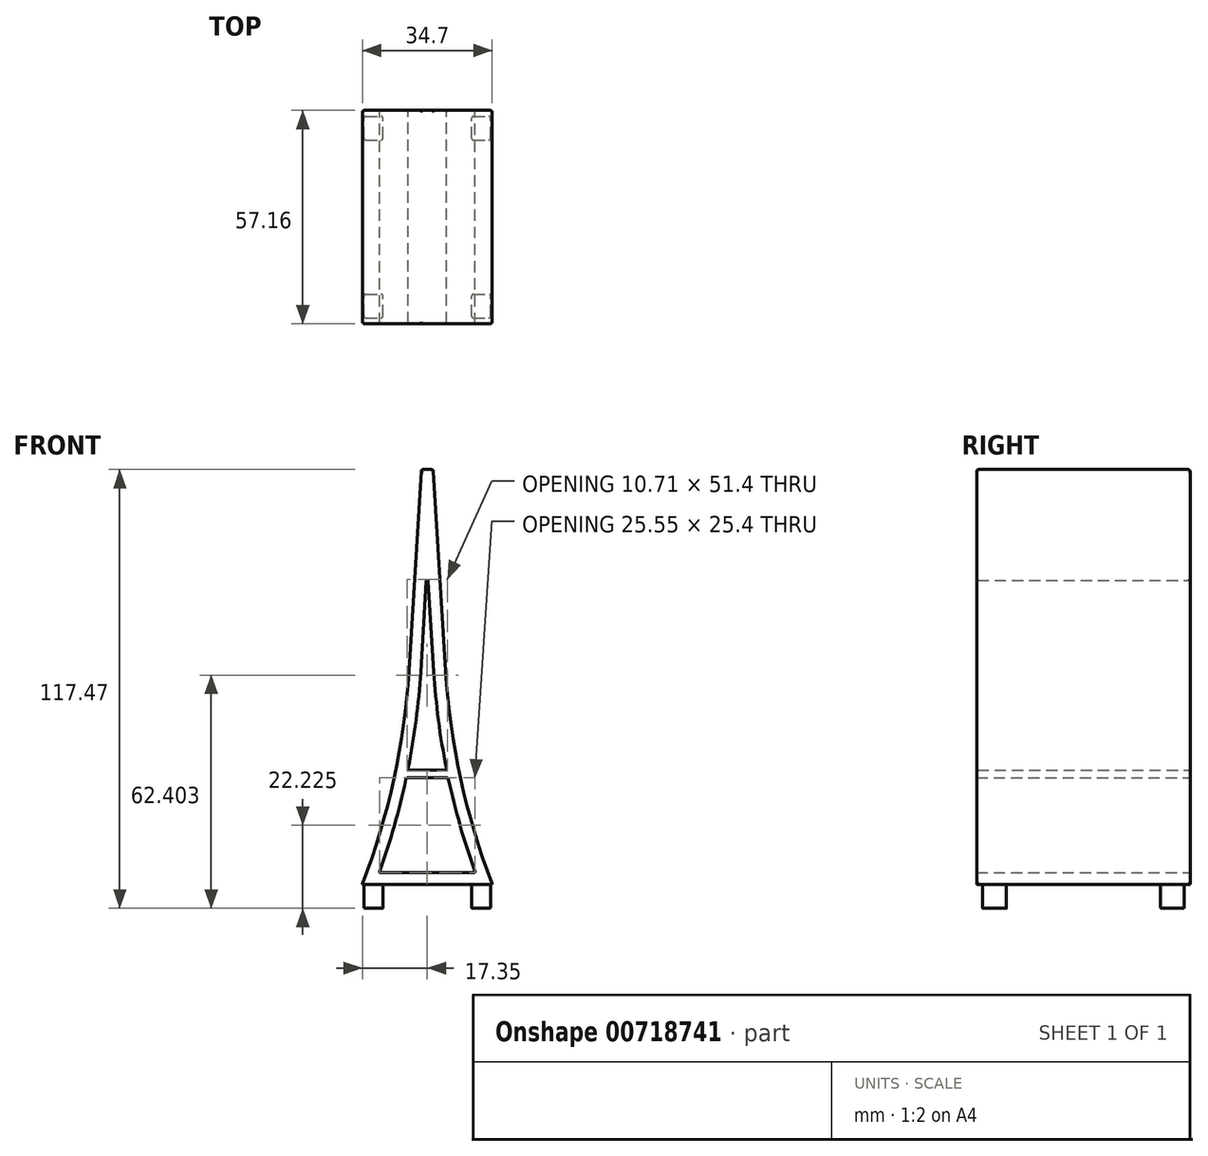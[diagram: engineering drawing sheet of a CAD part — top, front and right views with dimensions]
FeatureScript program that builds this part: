
annotation { "Feature Type Name" : "Feature", "Feature Type Description" : "" }
export const myFeature = defineFeature(function(context is Context, id is Id, definition is map)
    precondition{}
    {
        {
            var Q0;
            Q0=qCreatedBy(makeId("Front.planeOp"),FACE);
            var sketch = newSketch(context, id + "F0", { "sketchPlane" : qUnion([Q0])});
            skLineSegment(sketch, "E0", {"start": v(0, 0) * mm, "end": v(0, 107.5) * mm, "construction": true});
            skLineSegment(sketch, "E1", {"start": v(-17.46, 0) * mm, "end": v(17.46, 0) * mm});
            skLineSegment(sketch, "E2", {"start": v(-1.59, 111.13) * mm, "end": v(1.59, 111.13) * mm});
            skLineSegment(sketch, "E3", {"start": v(-1.59, 111.13) * mm, "end": v(-4.93, 57.15) * mm});
            skArc(sketch, "E4", {"start": v(-4.93, 57.15) * mm, "mid": v(-8.99, 28.1) * mm, "end": v(-17.46, 0) * mm});
            skLineSegment(sketch, "E5.MirrorCS", {"start": v(1.59, 111.13) * mm, "end": v(4.93, 57.15) * mm});
            skArc(sketch, "E6.MirrorCS", {"start": v(4.93, 57.15) * mm, "mid": v(8.99, 28.1) * mm, "end": v(17.46, 0) * mm});
            skLineSegment(sketch, "E7.top", {"start": v(-16.95, -6.35) * mm, "end": v(-11.87, -6.35) * mm});
            skLineSegment(sketch, "E7.left", {"start": v(-16.95, 0) * mm, "end": v(-16.95, -6.35) * mm});
            skLineSegment(sketch, "E7.right", {"start": v(-11.87, 0) * mm, "end": v(-11.87, -6.35) * mm});
            skLineSegment(sketch, "E8.MirrorCS", {"start": v(11.87, 0) * mm, "end": v(11.87, -6.35) * mm});
            skLineSegment(sketch, "E9.MirrorCS", {"start": v(16.95, -6.35) * mm, "end": v(11.87, -6.35) * mm});
            skLineSegment(sketch, "E10.MirrorCS", {"start": v(16.95, 0) * mm, "end": v(16.95, -6.35) * mm});
            skLineSegment(sketch, "E11", {"start": v(-12.88, 3.18) * mm, "end": v(12.88, 3.18) * mm});
            skLineSegment(sketch, "E12", {"start": v(0, 85.36) * mm, "end": v(-1.76, 56.95) * mm});
            skLineSegment(sketch, "E13.MirrorCS", {"start": v(0, 85.36) * mm, "end": v(1.76, 56.95) * mm});
            skArc(sketch, "E14", {"start": v(-1.76, 56.95) * mm, "mid": v(-5.4, 29.67) * mm, "end": v(-12.88, 3.17) * mm});
            skArc(sketch, "E15.MirrorCS", {"start": v(1.76, 56.95) * mm, "mid": v(5.4, 29.67) * mm, "end": v(12.88, 3.17) * mm});
            skLineSegment(sketch, "E16", {"start": v(-4.93, 57.15) * mm, "end": v(-1.76, 56.95) * mm, "construction": true});
            skLineSegment(sketch, "E17", {"start": v(-5.21, 30.6) * mm, "end": v(5.21, 30.6) * mm});
            skLineSegment(sketch, "E18", {"start": v(5.63, 28.58) * mm, "end": v(-5.63, 28.58) * mm});
            skSolve(sketch);
        }
        {
            var Q0;
            Q0=makeQuery(id+"F0.imprint","IMPRINT",FACE,{"disambiguationData":[TD([[makeQuery(id+"F0.imprint","IMPRINT",EDGE,{"derivedFrom":sQuery(id+"F0.wireOp",EDGE,"E1")}),1.0]])]});
            var Q1;
            {var subQ0=sQuery(id+"F0.wireOp",EDGE,"E17");Q1=makeQuery(id+"F0.imprint","IMPRINT",FACE,{"disambiguationData":[TD([[makeQuery(id+"F0.imprint","IMPRINT",EDGE,{"derivedFrom":subQ0}),-1.0]])]});}
            extrude(context, id + "F1", {"entities" : qUnion([Q0, Q1]), "endBound" : BoundingType.SYMMETRIC, "depth" : 57.15 * mm, "offsetDistance" : 25.4 * mm});
        }
        {
            var Q0;
            {var subQ0=sQuery(id+"F0.wireOp",EDGE,"E8.MirrorCS");Q0=makeQuery(id+"F0.imprint","IMPRINT",FACE,{"disambiguationData":[TD([[makeQuery(id+"F0.imprint","IMPRINT",EDGE,{"derivedFrom":subQ0}),1.0]])]});}
            var Q1;
            Q1=makeQuery(id+"F0.imprint","IMPRINT",FACE,{"disambiguationData":[TD([[makeQuery(id+"F0.imprint","IMPRINT",EDGE,{"derivedFrom":sQuery(id+"F0.wireOp",EDGE,"E7.top")}),1.0]])]});
            extrude(context, id + "F2", {"entities" : qUnion([Q0, Q1]), "operationType" : NewBodyOperationType.ADD, "endBound" : BoundingType.SYMMETRIC, "depth" : 53.97 * mm, "offsetDistance" : 25.4 * mm});
        }
        {
            var Q0;
            Q0=makeQuery(id+"F2.opExtrude","SWEPT_FACE",FACE,{"disambiguationData":[OSD([sQuery(id+"F0.wireOp",EDGE,"E10.MirrorCS")])]});
            var sketch = newSketch(context, id + "F3", { "sketchPlane" : qUnion([Q0])});
            skLineSegment(sketch, "E19", {"start": v(0, 0) * mm, "end": v(0, -6.35) * mm, "construction": true});
            skLineSegment(sketch, "E20.bottom", {"start": v(-20.64, 0) * mm, "end": v(20.64, 0) * mm});
            skLineSegment(sketch, "E20.top", {"start": v(-20.64, -6.35) * mm, "end": v(20.64, -6.35) * mm});
            skLineSegment(sketch, "E20.left", {"start": v(-20.64, 0) * mm, "end": v(-20.64, -6.35) * mm});
            skLineSegment(sketch, "E20.right", {"start": v(20.64, 0) * mm, "end": v(20.64, -6.35) * mm});
            skSolve(sketch);
        }
        {
            var Q0;
            Q0=makeQuery(id+"F3.imprint","IMPRINT",FACE,{"disambiguationData":[TD([[makeQuery(id+"F3.imprint","IMPRINT",EDGE,{"derivedFrom":sQuery(id+"F3.wireOp",EDGE,"E20.bottom")}),-1.0]])]});
            extrude(context, id + "F4", {"entities" : qUnion([Q0]), "operationType" : NewBodyOperationType.REMOVE, "endBound" : BoundingType.THROUGH_ALL, "oppositeDirection" : true, "depth" : 25.4 * mm, "offsetDistance" : 25.4 * mm});
        }
        {
            var Q0;
            Q0=makeQuery(id+"F1.opExtrude","CAP_EDGE",EDGE,{"disambiguationData":[OSD([sQuery(id+"F0.wireOp",EDGE,"E5.MirrorCS")])],"isStart":false});
            var Q1;
            Q1=makeQuery(id+"F1.opExtrude","CAP_EDGE",EDGE,{"disambiguationData":[OSD([sQuery(id+"F0.wireOp",EDGE,"E3")])],"isStart":false});
            var Q2;
            Q2=makeQuery(id+"F1.opExtrude","CAP_EDGE",EDGE,{"disambiguationData":[OSD([sQuery(id+"F0.wireOp",EDGE,"E5.MirrorCS")])],"isStart":true});
            var Q3;
            Q3=makeQuery(id+"F1.opExtrude","CAP_EDGE",EDGE,{"disambiguationData":[OSD([sQuery(id+"F0.wireOp",EDGE,"E3")])],"isStart":true});
            fillet(context, id + "F5", {"entities" : qUnion([Q0, Q1, Q2, Q3]), "radius" : 0.5 * mm, "tangentPropagation" : true, "allowEdgeOverflow" : false});
        }
        {
            var Q0;
            Q0=makeQuery(id+"F1.opExtrude","SWEPT_EDGE",EDGE,{"disambiguationData":[OSD([sQuery(id+"F0.wireOp",EDGE,"E2"),sQuery(id+"F0.wireOp",EDGE,"E3")])]});
            fillet(context, id + "F6", {"entities" : qUnion([Q0]), "radius" : 0.5 * mm, "tangentPropagation" : true, "allowEdgeOverflow" : false});
        }
        {
            var Q0;
            Q0=makeQuery(id+"F1.opExtrude","SWEPT_EDGE",EDGE,{"disambiguationData":[OSD([sQuery(id+"F0.wireOp",EDGE,"E11"),sQuery(id+"F0.wireOp",EDGE,"E15.MirrorCS")])]});
            var Q1;
            Q1=makeQuery(id+"F1.opExtrude","SWEPT_EDGE",EDGE,{"disambiguationData":[OSD([sQuery(id+"F0.wireOp",EDGE,"E11"),sQuery(id+"F0.wireOp",EDGE,"E14")])]});
            var Q2;
            Q2=makeQuery(id+"F1.opExtrude","SWEPT_EDGE",EDGE,{"disambiguationData":[OSD([sQuery(id+"F0.wireOp",EDGE,"E12"),sQuery(id+"F0.wireOp",EDGE,"E13.MirrorCS")])]});
            fillet(context, id + "F7", {"entities" : qUnion([Q0, Q1, Q2]), "radius" : 0.25 * mm, "tangentPropagation" : true, "allowEdgeOverflow" : false});
        }
        {
            var Q0;
            Q0=makeQuery(id+"F1.opExtrude","SWEPT_EDGE",EDGE,{"disambiguationData":[OSD([sQuery(id+"F0.wireOp",EDGE,"E14"),sQuery(id+"F0.wireOp",EDGE,"E17")])]});
            var Q1;
            Q1=makeQuery(id+"F1.opExtrude","SWEPT_EDGE",EDGE,{"disambiguationData":[OSD([sQuery(id+"F0.wireOp",EDGE,"E15.MirrorCS"),sQuery(id+"F0.wireOp",EDGE,"E17")])]});
            var Q2;
            Q2=makeQuery(id+"F1.opExtrude","SWEPT_EDGE",EDGE,{"disambiguationData":[OSD([sQuery(id+"F0.wireOp",EDGE,"E15.MirrorCS"),sQuery(id+"F0.wireOp",EDGE,"E18")])]});
            var Q3;
            Q3=makeQuery(id+"F1.opExtrude","SWEPT_EDGE",EDGE,{"disambiguationData":[OSD([sQuery(id+"F0.wireOp",EDGE,"E14"),sQuery(id+"F0.wireOp",EDGE,"E18")])]});
            fillet(context, id + "F8", {"entities" : qUnion([Q0, Q1, Q2, Q3]), "radius" : 0.5 * mm, "tangentPropagation" : true, "allowEdgeOverflow" : false});
        }
        {
            var Q0;
            Q0=makeQuery(id+"F1.opExtrude","CAP_EDGE",EDGE,{"disambiguationData":[OSD([sQuery(id+"F0.wireOp",EDGE,"E13.MirrorCS")])],"isStart":true});
            var Q1;
            Q1=makeQuery(id+"F1.opExtrude","CAP_EDGE",EDGE,{"disambiguationData":[OSD([sQuery(id+"F0.wireOp",EDGE,"E13.MirrorCS")])],"isStart":false});
            var Q2;
            {var subQ0=sQuery(id+"F0.wireOp",EDGE,"E14");Q2=makeQuery(id+"F1.opExtrude","CAP_EDGE",EDGE,{"disambiguationData":[OSD([subQ0]),TDD([makeQuery(id+"F0.imprint","IMPRINT",EDGE,{"disambiguationData":[TD([[makeQuery(id+"F0.imprint","INTERSECT",VERTEX,{"derivedFrom":[sQuery(id+"F0.wireOp",EDGE,"E11"),subQ0]}),1.0]])],"derivedFrom":subQ0})])],"isStart":true});}
            var Q3;
            {var subQ0=sQuery(id+"F0.wireOp",EDGE,"E14");Q3=makeQuery(id+"F1.opExtrude","CAP_EDGE",EDGE,{"disambiguationData":[OSD([subQ0]),TDD([makeQuery(id+"F0.imprint","IMPRINT",EDGE,{"disambiguationData":[TD([[makeQuery(id+"F0.imprint","INTERSECT",VERTEX,{"derivedFrom":[sQuery(id+"F0.wireOp",EDGE,"E11"),subQ0]}),1.0]])],"derivedFrom":subQ0})])],"isStart":false});}
            fillet(context, id + "F9", {"entities" : qUnion([Q0, Q1, Q2, Q3]), "radius" : 0.25 * mm, "tangentPropagation" : true, "allowEdgeOverflow" : false});
        }
        {
            var Q0;
            Q0=makeQuery(id+"F1.opExtrude","CAP_EDGE",EDGE,{"disambiguationData":[OSD([sQuery(id+"F0.wireOp",EDGE,"E1")])],"isStart":false});
            fillet(context, id + "F10", {"entities" : qUnion([Q0]), "radius" : 0.25 * mm, "tangentPropagation" : true, "allowEdgeOverflow" : false});
        }
        {
            var Q0;
            Q0=makeQuery(id+"F2.opExtrude","CAP_EDGE",EDGE,{"disambiguationData":[OSD([sQuery(id+"F0.wireOp",EDGE,"E7.left")])],"isStart":false});
            var Q1;
            Q1=makeQuery(id+"F2.opExtrude","CAP_EDGE",EDGE,{"disambiguationData":[OSD([sQuery(id+"F0.wireOp",EDGE,"E7.right")])],"isStart":false});
            var Q2;
            Q2=makeQuery(id+"F4.boolean.opBoolean","INTERSECT",EDGE,{"derivedFrom":[makeQuery(id+"F2.opExtrude","SWEPT_FACE",FACE,{"disambiguationData":[OSD([sQuery(id+"F0.wireOp",EDGE,"E7.left")])]}),makeQuery(id+"F4.opExtrude","SWEPT_FACE",FACE,{"disambiguationData":[OSD([sQuery(id+"F3.wireOp",EDGE,"E20.left")])]})]});
            var Q3;
            Q3=makeQuery(id+"F4.boolean.opBoolean","INTERSECT",EDGE,{"derivedFrom":[makeQuery(id+"F2.opExtrude","SWEPT_FACE",FACE,{"disambiguationData":[OSD([sQuery(id+"F0.wireOp",EDGE,"E7.right")])]}),makeQuery(id+"F4.opExtrude","SWEPT_FACE",FACE,{"disambiguationData":[OSD([sQuery(id+"F3.wireOp",EDGE,"E20.left")])]})]});
            var Q4;
            Q4=makeQuery(id+"F4.boolean.opBoolean","COPY",EDGE,{"derivedFrom":makeQuery(id+"F4.opExtrude","CAP_EDGE",EDGE,{"disambiguationData":[OSD([sQuery(id+"F3.wireOp",EDGE,"E20.left")])],"isStart":true})});
            var Q5;
            Q5=makeQuery(id+"F4.boolean.opBoolean","INTERSECT",EDGE,{"derivedFrom":[makeQuery(id+"F2.opExtrude","SWEPT_FACE",FACE,{"disambiguationData":[OSD([sQuery(id+"F0.wireOp",EDGE,"E8.MirrorCS")])]}),makeQuery(id+"F4.opExtrude","SWEPT_FACE",FACE,{"disambiguationData":[OSD([sQuery(id+"F3.wireOp",EDGE,"E20.left")])]})]});
            var Q6;
            Q6=makeQuery(id+"F2.opExtrude","CAP_EDGE",EDGE,{"disambiguationData":[OSD([sQuery(id+"F0.wireOp",EDGE,"E8.MirrorCS")])],"isStart":false});
            var Q7;
            Q7=makeQuery(id+"F2.opExtrude","CAP_EDGE",EDGE,{"disambiguationData":[OSD([sQuery(id+"F0.wireOp",EDGE,"E10.MirrorCS")])],"isStart":false});
            var Q8;
            Q8=makeQuery(id+"F2.opExtrude","CAP_EDGE",EDGE,{"disambiguationData":[OSD([sQuery(id+"F0.wireOp",EDGE,"E10.MirrorCS")])],"isStart":true});
            var Q9;
            Q9=makeQuery(id+"F4.boolean.opBoolean","COPY",EDGE,{"derivedFrom":makeQuery(id+"F4.opExtrude","CAP_EDGE",EDGE,{"disambiguationData":[OSD([sQuery(id+"F3.wireOp",EDGE,"E20.right")])],"isStart":true})});
            var Q10;
            Q10=makeQuery(id+"F2.opExtrude","CAP_EDGE",EDGE,{"disambiguationData":[OSD([sQuery(id+"F0.wireOp",EDGE,"E8.MirrorCS")])],"isStart":true});
            var Q11;
            Q11=makeQuery(id+"F4.boolean.opBoolean","INTERSECT",EDGE,{"derivedFrom":[makeQuery(id+"F2.opExtrude","SWEPT_FACE",FACE,{"disambiguationData":[OSD([sQuery(id+"F0.wireOp",EDGE,"E7.right")])]}),makeQuery(id+"F4.opExtrude","SWEPT_FACE",FACE,{"disambiguationData":[OSD([sQuery(id+"F3.wireOp",EDGE,"E20.right")])]})]});
            var Q12;
            Q12=makeQuery(id+"F2.opExtrude","CAP_EDGE",EDGE,{"disambiguationData":[OSD([sQuery(id+"F0.wireOp",EDGE,"E7.right")])],"isStart":true});
            var Q13;
            Q13=makeQuery(id+"F2.opExtrude","CAP_EDGE",EDGE,{"disambiguationData":[OSD([sQuery(id+"F0.wireOp",EDGE,"E7.left")])],"isStart":true});
            var Q14;
            Q14=makeQuery(id+"F4.boolean.opBoolean","INTERSECT",EDGE,{"derivedFrom":[makeQuery(id+"F2.opExtrude","SWEPT_FACE",FACE,{"disambiguationData":[OSD([sQuery(id+"F0.wireOp",EDGE,"E7.left")])]}),makeQuery(id+"F4.opExtrude","SWEPT_FACE",FACE,{"disambiguationData":[OSD([sQuery(id+"F3.wireOp",EDGE,"E20.right")])]})]});
            var Q15;
            Q15=makeQuery(id+"F4.boolean.opBoolean","INTERSECT",EDGE,{"derivedFrom":[makeQuery(id+"F2.opExtrude","SWEPT_FACE",FACE,{"disambiguationData":[OSD([sQuery(id+"F0.wireOp",EDGE,"E8.MirrorCS")])]}),makeQuery(id+"F4.opExtrude","SWEPT_FACE",FACE,{"disambiguationData":[OSD([sQuery(id+"F3.wireOp",EDGE,"E20.right")])]})]});
            fillet(context, id + "F11", {"entities" : qUnion([Q0, Q1, Q2, Q3, Q4, Q5, Q6, Q7, Q8, Q9, Q10, Q11, Q12, Q13, Q14, Q15]), "radius" : 0.5 * mm, "tangentPropagation" : true, "allowEdgeOverflow" : false});
        }
        {
            var Q0;
            Q0=makeQuery(id+"F2.opExtrude","CAP_EDGE",EDGE,{"disambiguationData":[OSD([sQuery(id+"F0.wireOp",EDGE,"E7.top")])],"isStart":true});
            var Q1;
            Q1=makeQuery(id+"F2.opExtrude","CAP_EDGE",EDGE,{"disambiguationData":[OSD([sQuery(id+"F0.wireOp",EDGE,"E9.MirrorCS")])],"isStart":true});
            var Q2;
            {var subQ0=sQuery(id+"F3.wireOp",EDGE,"E20.left");Q2=makeQuery(id+"F4.boolean.opBoolean","COPY",EDGE,{"disambiguationData":[topologyDisambiguationEdgeConnected([makeQuery(id+"F2.opExtrude","SWEPT_FACE",FACE,{"disambiguationData":[OSD([sQuery(id+"F0.wireOp",EDGE,"E7.top")])]})])],"derivedFrom":makeQuery(id+"F4.opExtrude","SWEPT_EDGE",EDGE,{"disambiguationData":[OSD([sQuery(id+"F0.wireOp",EDGE,"E9.MirrorCS"),sQuery(id+"F0.wireOp",EDGE,"E10.MirrorCS"),sQuery(id+"F3.wireOp",EDGE,"E20.top"),subQ0])]})});}
            var Q3;
            {var subQ0=sQuery(id+"F0.wireOp",EDGE,"E9.MirrorCS");var subQ1=sQuery(id+"F3.wireOp",EDGE,"E20.left");Q3=makeQuery(id+"F4.boolean.opBoolean","COPY",EDGE,{"disambiguationData":[topologyDisambiguationEdgeConnected([makeQuery(id+"F2.opExtrude","SWEPT_FACE",FACE,{"disambiguationData":[OSD([subQ0])]})])],"derivedFrom":makeQuery(id+"F4.opExtrude","SWEPT_EDGE",EDGE,{"disambiguationData":[OSD([subQ0,sQuery(id+"F0.wireOp",EDGE,"E10.MirrorCS"),sQuery(id+"F3.wireOp",EDGE,"E20.top"),subQ1])]})});}
            fillet(context, id + "F12", {"entities" : qUnion([Q0, Q1, Q2, Q3]), "radius" : 0.25 * mm, "tangentPropagation" : true, "allowEdgeOverflow" : false});
        }
    });
